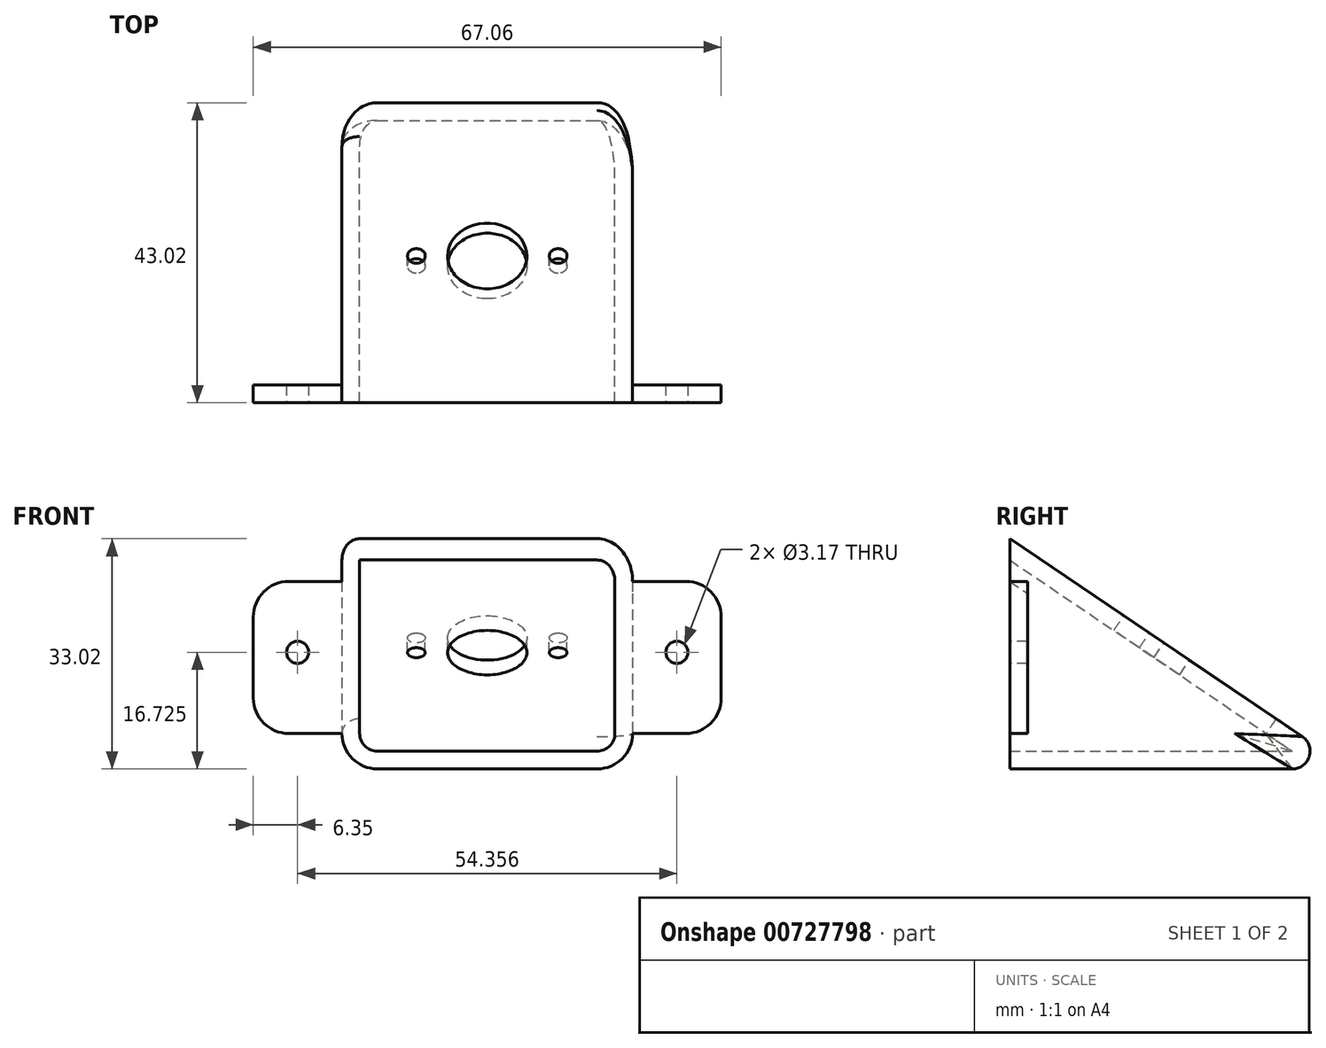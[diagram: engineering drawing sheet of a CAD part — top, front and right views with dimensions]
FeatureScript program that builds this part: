
annotation { "Feature Type Name" : "Feature", "Feature Type Description" : "" }
export const myFeature = defineFeature(function(context is Context, id is Id, definition is map)
    precondition{}
    {
        {
            var Q0;
            Q0=qCreatedBy(makeId("Top.planeOp"),FACE);
            var sketch = newSketch(context, id + "F0", { "sketchPlane" : qUnion([Q0])});
            skLineSegment(sketch, "E0.bottom", {"start": v(-40.64, 54.85) * mm, "end": v(1.02, 54.85) * mm});
            skLineSegment(sketch, "E0.top", {"start": v(-40.64, 6.08) * mm, "end": v(1.02, 6.08) * mm});
            skLineSegment(sketch, "E0.left", {"start": v(-40.64, 54.85) * mm, "end": v(-40.64, 6.08) * mm});
            skLineSegment(sketch, "E0.right", {"start": v(1.02, 54.85) * mm, "end": v(1.02, 6.08) * mm});
            skSolve(sketch);
        }
        {
            var Q0;
            Q0=makeQuery(id+"F0.imprint","IMPRINT",FACE,{"disambiguationData":[TD([[makeQuery(id+"F0.imprint","IMPRINT",EDGE,{"derivedFrom":sQuery(id+"F0.wireOp",EDGE,"E0.bottom")}),-1.0]])]});
            extrude(context, id + "F1", {"entities" : qUnion([Q0]), "depth" : 33.02 * mm, "offsetDistance" : 25.4 * mm});
        }
        {
            var Q0;
            Q0=makeQuery(id+"F1.opExtrude","SWEPT_FACE",FACE,{"disambiguationData":[OSD([sQuery(id+"F0.wireOp",EDGE,"E0.left")])]});
            var sketch = newSketch(context, id + "F2", { "sketchPlane" : qUnion([Q0])});
            skLineSegment(sketch, "E1", {"start": v(-54.85, 0) * mm, "end": v(-6.08, 33.02) * mm});
            skSolve(sketch);
        }
        {
            var Q0;
            Q0=makeQuery(id+"F2.imprint","IMPRINT",FACE,{"disambiguationData":[TD([[makeQuery(id+"F2.imprint","IMPRINT",EDGE,{"derivedFrom":sQuery(id+"F2.wireOp",EDGE,"E1")}),1.0]])]});
            extrude(context, id + "F3", {"entities" : qUnion([Q0]), "operationType" : NewBodyOperationType.REMOVE, "oppositeDirection" : true, "depth" : 90.17 * mm, "offsetDistance" : 25.4 * mm});
        }
        {
            var Q0;
            Q0=makeQuery(id+"F1.opExtrude","CAP_EDGE",EDGE,{"disambiguationData":[OSD([sQuery(id+"F0.wireOp",EDGE,"E0.right")])],"isStart":true});
            var Q1;
            Q1=makeQuery(id+"F3.boolean.opBoolean","INTERSECT",EDGE,{"derivedFrom":[makeQuery(id+"F1.opExtrude","SWEPT_FACE",FACE,{"disambiguationData":[OSD([sQuery(id+"F0.wireOp",EDGE,"E0.right")])]}),makeQuery(id+"F3.opExtrude","SWEPT_FACE",FACE,{"disambiguationData":[OSD([sQuery(id+"F2.wireOp",EDGE,"E1")])]})]});
            var Q2;
            Q2=makeQuery(id+"F3.boolean.opBoolean","COPY",EDGE,{"derivedFrom":makeQuery(id+"F3.opExtrude","CAP_EDGE",EDGE,{"disambiguationData":[OSD([sQuery(id+"F2.wireOp",EDGE,"E1")])],"isStart":true})});
            var Q3;
            Q3=makeQuery(id+"F1.opExtrude","CAP_EDGE",EDGE,{"disambiguationData":[OSD([sQuery(id+"F0.wireOp",EDGE,"E0.left")])],"isStart":true});
            fillet(context, id + "F4", {"entities" : qUnion([Q0, Q1, Q2, Q3]), "radius" : 5.08 * mm, "tangentPropagation" : true, "allowEdgeOverflow" : false});
        }
        {
            var Q0;
            {var subQ0=sQuery(id+"F0.wireOp",EDGE,"E0.bottom");Q0=makeQuery(id+"F3.boolean.opBoolean","MERGE",EDGE,{"derivedFrom":[makeQuery(id+"F1.opExtrude","CAP_EDGE",EDGE,{"disambiguationData":[OSD([subQ0])],"isStart":true}),makeQuery(id+"F3.opExtrude","SWEPT_EDGE",EDGE,{"disambiguationData":[OSD([subQ0,sQuery(id+"F0.wireOp",EDGE,"E0.left"),sQuery(id+"F2.wireOp",EDGE,"E1")])]})]});}
            fillet(context, id + "F5", {"entities" : qUnion([Q0]), "radius" : 2.54 * mm, "tangentPropagation" : true, "allowEdgeOverflow" : false});
        }
        {
            var Q0;
            Q0=makeQuery(id+"F3.boolean.opBoolean","COPY",FACE,{"derivedFrom":makeQuery(id+"F3.opExtrude","SWEPT_FACE",FACE,{"disambiguationData":[OSD([sQuery(id+"F2.wireOp",EDGE,"E1")])]})});
            var sketch = newSketch(context, id + "F6", { "sketchPlane" : qUnion([Q0])});
            skCircle(sketch, "E2", {"center": v(-9.65, 11.92) * mm, "radius": 1.27 * mm});
            skCircle(sketch, "E3", {"center": v(-29.97, 11.92) * mm, "radius": 1.27 * mm});
            skCircle(sketch, "E4", {"center": v(-19.81, 11.92) * mm, "radius": 5.67 * mm});
            skSolve(sketch);
        }
        {
            var Q0;
            Q0=makeQuery(id+"F1.opExtrude","SWEPT_FACE",FACE,{"disambiguationData":[OSD([sQuery(id+"F0.wireOp",EDGE,"E0.top")])]});
            shell(context, id + "F7", {"entities" : qUnion([Q0]), "thickness" : 2.54 * mm});
        }
        {
            var Q0;
            Q0=makeQuery(id+"F1.opExtrude","SWEPT_FACE",FACE,{"disambiguationData":[OSD([sQuery(id+"F0.wireOp",EDGE,"E0.top")])]});
            var sketch = newSketch(context, id + "F8", { "sketchPlane" : qUnion([Q0])});
            skLineSegment(sketch, "E5.bottom", {"start": v(1.02, 26.89) * mm, "end": v(13.72, 26.89) * mm});
            skLineSegment(sketch, "E5.top", {"start": v(1.02, 5.08) * mm, "end": v(13.72, 5.08) * mm});
            skLineSegment(sketch, "E5.left", {"start": v(1.02, 26.89) * mm, "end": v(1.02, 5.08) * mm});
            skLineSegment(sketch, "E5.right", {"start": v(13.72, 26.89) * mm, "end": v(13.72, 5.08) * mm});
            skLineSegment(sketch, "E6.bottom", {"start": v(-40.64, 26.89) * mm, "end": v(-53.34, 26.89) * mm});
            skLineSegment(sketch, "E6.top", {"start": v(-40.64, 5.08) * mm, "end": v(-53.34, 5.08) * mm});
            skLineSegment(sketch, "E6.left", {"start": v(-40.64, 26.89) * mm, "end": v(-40.64, 5.08) * mm});
            skLineSegment(sketch, "E6.right", {"start": v(-53.34, 26.89) * mm, "end": v(-53.34, 5.08) * mm});
            skSolve(sketch);
        }
        {
            var Q0;
            Q0=makeQuery(id+"F8.imprint","IMPRINT",FACE,{"disambiguationData":[TD([[makeQuery(id+"F8.imprint","IMPRINT",EDGE,{"derivedFrom":sQuery(id+"F8.wireOp",EDGE,"E6.bottom")}),1.0]])]});
            var Q1;
            Q1=makeQuery(id+"F8.imprint","IMPRINT",FACE,{"disambiguationData":[TD([[makeQuery(id+"F8.imprint","IMPRINT",EDGE,{"derivedFrom":sQuery(id+"F8.wireOp",EDGE,"E5.bottom")}),-1.0]])]});
            extrude(context, id + "F9", {"entities" : qUnion([Q0, Q1]), "operationType" : NewBodyOperationType.ADD, "oppositeDirection" : true, "depth" : 2.54 * mm, "offsetDistance" : 25.4 * mm});
        }
        {
            var Q0;
            Q0=makeQuery(id+"F9.boolean.opBoolean","MERGE",FACE,{"derivedFrom":[makeQuery(id+"F1.opExtrude","SWEPT_FACE",FACE,{"disambiguationData":[OSD([sQuery(id+"F0.wireOp",EDGE,"E0.top")])]}),makeQuery(id+"F9.opExtrude","CAP_FACE",FACE,{"disambiguationData":[OSD([sQuery(id+"F8.wireOp",EDGE,"E5.bottom"),sQuery(id+"F8.wireOp",EDGE,"E5.top"),sQuery(id+"F8.wireOp",EDGE,"E5.left"),sQuery(id+"F8.wireOp",EDGE,"E5.right")])],"isStart":true}),makeQuery(id+"F9.opExtrude","CAP_FACE",FACE,{"disambiguationData":[OSD([sQuery(id+"F8.wireOp",EDGE,"E6.bottom"),sQuery(id+"F8.wireOp",EDGE,"E6.top"),sQuery(id+"F8.wireOp",EDGE,"E6.left"),sQuery(id+"F8.wireOp",EDGE,"E6.right")])],"isStart":true})]});
            var sketch = newSketch(context, id + "F10", { "sketchPlane" : qUnion([Q0])});
            skCircle(sketch, "E7", {"center": v(-46.99, 16.73) * mm, "radius": 1.59 * mm});
            skCircle(sketch, "E8", {"center": v(7.37, 16.73) * mm, "radius": 1.59 * mm});
            skSolve(sketch);
        }
        {
            var Q0;
            Q0=makeQuery(id+"F10.imprint","IMPRINT",FACE,{"disambiguationData":[TD([[makeQuery(id+"F10.imprint","IMPRINT",EDGE,{"derivedFrom":sQuery(id+"F10.wireOp",EDGE,"E7")}),1.0]])]});
            var Q1;
            Q1=makeQuery(id+"F10.imprint","IMPRINT",FACE,{"disambiguationData":[TD([[makeQuery(id+"F10.imprint","IMPRINT",EDGE,{"derivedFrom":sQuery(id+"F10.wireOp",EDGE,"E8")}),1.0]])]});
            var Q2;
            Q2=sQuery(id+"F10.wireOp",EDGE,"9ivVBFSL-sHKy-JtaL-dwiv-NxNFrRwKzWoG");
            extrude(context, id + "F11", {"entities" : qUnion([Q0, Q1]), "operationType" : NewBodyOperationType.REMOVE, "surfaceEntities" : qUnion([Q2]), "oppositeDirection" : true, "depth" : 5.08 * mm, "offsetDistance" : 25.4 * mm});
        }
        {
            var Q0;
            Q0=makeQuery(id+"F9.opExtrude","SWEPT_EDGE",EDGE,{"disambiguationData":[OSD([sQuery(id+"F8.wireOp",EDGE,"E6.bottom"),sQuery(id+"F8.wireOp",EDGE,"E6.right")])]});
            var Q1;
            Q1=makeQuery(id+"F9.opExtrude","SWEPT_EDGE",EDGE,{"disambiguationData":[OSD([sQuery(id+"F8.wireOp",EDGE,"E5.bottom"),sQuery(id+"F8.wireOp",EDGE,"E5.right")])]});
            var Q2;
            Q2=makeQuery(id+"F9.opExtrude","SWEPT_EDGE",EDGE,{"disambiguationData":[OSD([sQuery(id+"F8.wireOp",EDGE,"E6.top"),sQuery(id+"F8.wireOp",EDGE,"E6.right")])]});
            var Q3;
            Q3=makeQuery(id+"F9.opExtrude","SWEPT_EDGE",EDGE,{"disambiguationData":[OSD([sQuery(id+"F8.wireOp",EDGE,"E5.top"),sQuery(id+"F8.wireOp",EDGE,"E5.right")])]});
            fillet(context, id + "F12", {"entities" : qUnion([Q0, Q1, Q2, Q3]), "radius" : 5.08 * mm, "tangentPropagation" : true, "allowEdgeOverflow" : false});
        }
        {
            var Q0;
            Q0=makeQuery(id+"F6.imprint","IMPRINT",FACE,{"disambiguationData":[TD([[makeQuery(id+"F6.imprint","IMPRINT",EDGE,{"derivedFrom":sQuery(id+"F6.wireOp",EDGE,"E3")}),1.0]])]});
            var Q1;
            Q1=makeQuery(id+"F6.imprint","IMPRINT",FACE,{"disambiguationData":[TD([[makeQuery(id+"F6.imprint","IMPRINT",EDGE,{"derivedFrom":sQuery(id+"F6.wireOp",EDGE,"E4")}),1.0]])]});
            var Q2;
            Q2=makeQuery(id+"F6.imprint","IMPRINT",FACE,{"disambiguationData":[TD([[makeQuery(id+"F6.imprint","IMPRINT",EDGE,{"derivedFrom":sQuery(id+"F6.wireOp",EDGE,"E2")}),1.0]])]});
            extrude(context, id + "F13", {"entities" : qUnion([Q0, Q1, Q2]), "operationType" : NewBodyOperationType.REMOVE, "oppositeDirection" : true, "depth" : 7.62 * mm, "offsetDistance" : 25.4 * mm});
        }
    });
